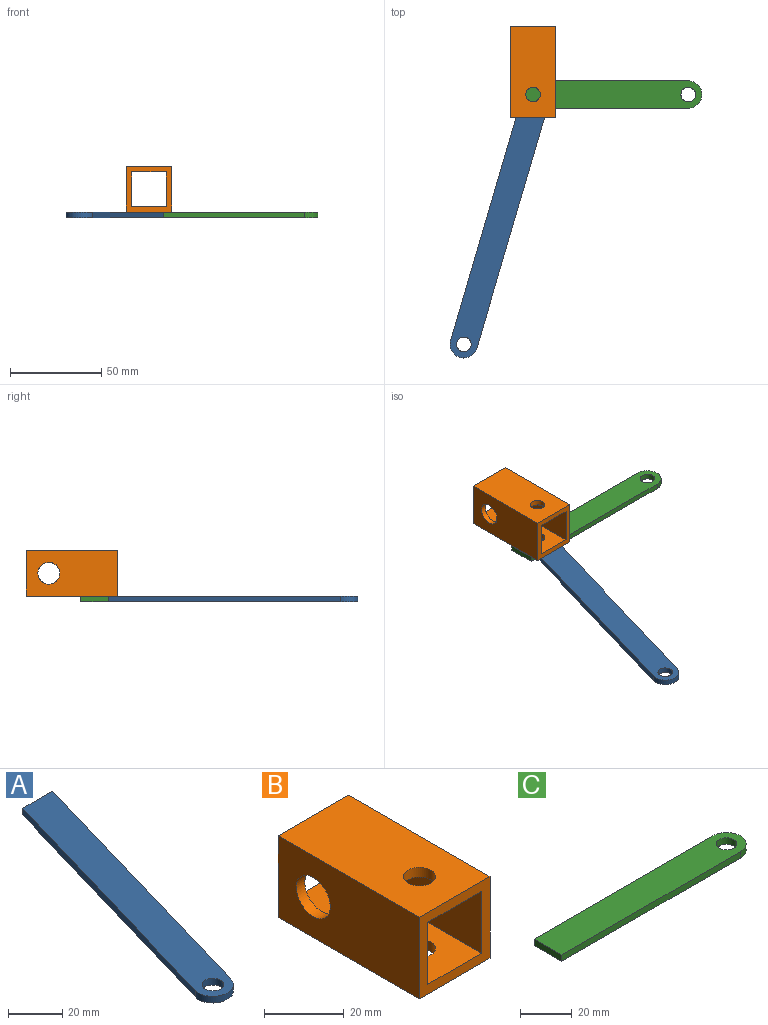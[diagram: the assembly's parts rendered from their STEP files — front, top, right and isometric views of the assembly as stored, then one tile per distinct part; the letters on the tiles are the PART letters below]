
ASSEMBLY  parts=3 mates=2
PART A: 7 faces, bbox 53.2x136.7x3 mm
  f0: plane 127.14x37.27mm, normal (-0.96,0.28,0), area 397.5mm2, adj f1,f4,f5,f6
  f1: cylinder r=7.5mm len=14.7mm, axis (0,0,-1), area 70.7mm2, adj f0,f2,f5,f6
  f2: plane 131.36x38.5mm, normal (0.96,-0.28,0), area 410.6mm2, adj f1,f4,f5,f6
  f3: cylinder r=4mm len=8mm, axis (0,0,-1), area 75.4mm2, adj f5,f6
  f4: plane 15.63x3mm, normal (0,1,0), area 46.9mm2, adj f0,f2,f5,f6
  f5: plane 136.75x53.2mm, normal (0,0,1), area 2058.4mm2, adj f0,f1,f2,f3,f4
  f6: plane 136.75x53.2mm, normal (0,0,-1), area 2058.4mm2, adj f0,f1,f2,f3,f4
PART B: 14 faces, bbox 25x50x25 mm
  f0: cylinder r=6mm len=12mm, axis (-1,0,0), area 113.1mm2, adj f3,f9
  f1: plane 50x25mm, normal (-1,0,0), area 1136.9mm2, adj f2,f4,f5,f6,f7
  f2: plane 25x25mm, normal (0,-1,0), area 264mm2, adj f1,f3,f5,f6,f8,f9,f10,f11
  f3: plane 50x25mm, normal (1,0,0), area 1136.9mm2, adj f0,f2,f4,f5,f6
  f4: plane 25x25mm, normal (0,1,0), area 264mm2, adj f1,f3,f5,f6,f8,f9,f10,f11
  f5: plane 50x25mm, normal (0,0,-1), area 1199.7mm2, adj f1,f2,f3,f4,f13
  f6: plane 50x25mm, normal (0,0,1), area 1199.7mm2, adj f1,f2,f3,f4,f12
  f7: cylinder r=6mm len=12mm, axis (-1,0,0), area 113.1mm2, adj f1,f8
  f8: plane 50x19mm, normal (1,0,0), area 836.9mm2, adj f2,f4,f7,f10,f11
  f9: plane 50x19mm, normal (-1,0,0), area 836.9mm2, adj f0,f2,f4,f10,f11
  f10: plane 50x19mm, normal (0,0,1), area 899.7mm2, adj f2,f4,f8,f9,f13
  f11: plane 50x19mm, normal (0,0,-1), area 899.7mm2, adj f2,f4,f8,f9,f12
  f12: cylinder r=4mm len=8mm, axis (0,0,1), area 75.4mm2, adj f6,f11
  f13: cylinder r=4mm len=8mm, axis (0,0,1), area 75.4mm2, adj f5,f10
PART C: 7 faces, bbox 105x15x3 mm
  f0: plane 97.5x3mm, normal (0,-1,0), area 292.5mm2, adj f1,f4,f5,f6
  f1: cylinder r=7.5mm len=15mm, axis (0,0,-1), area 70.7mm2, adj f0,f2,f5,f6
  f2: plane 97.5x3mm, normal (0,1,0), area 292.5mm2, adj f1,f4,f5,f6
  f3: cylinder r=4mm len=8mm, axis (0,0,-1), area 75.4mm2, adj f5,f6
  f4: plane 15x3mm, normal (-1,0,0), area 45mm2, adj f0,f2,f5,f6
  f5: plane 105x15mm, normal (0,0,1), area 1500.6mm2, adj f0,f1,f2,f3,f4
  f6: plane 105x15mm, normal (0,0,-1), area 1500.6mm2, adj f0,f1,f2,f3,f4
PLACE A t=(-6.84,-7.16,0.34)mm
PLACE B t=(-9.04,-7.16,3.34)mm
PLACE C t=(-9.04,-7.16,0.34)mm
MATE fastened A.f5 <-> B.f5  axis (0,0,1) through (-9.04,-14.66,3.34)mm
MATE fastened C.f5 <-> B.f5  axis (0,0,1) through (-21.54,-7.16,3.34)mm
